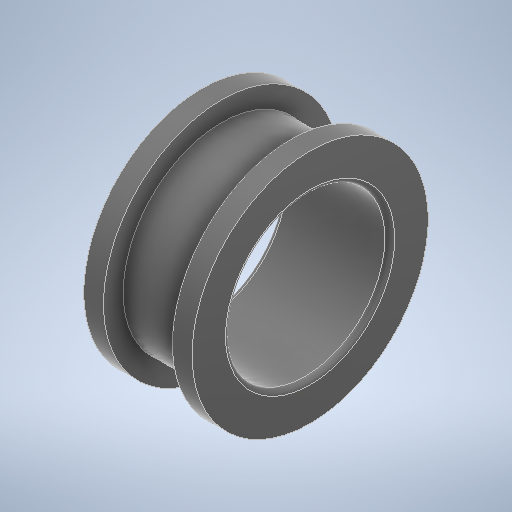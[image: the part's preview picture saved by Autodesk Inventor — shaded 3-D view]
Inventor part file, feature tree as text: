
AUTODESK INVENTOR PART (.ipt)
format: ipt  version: 2025.1 (Build 291241020, 241B)  size: 620,544 bytes
history: native  units: mm
features: revolve x1, mirror x1, fillet x1, sketch x1
ambient origin geometry x8: Origin, YZ Plane, XZ Plane, XY Plane, X Axis, Y Axis, Z Axis, Center Point
bodies: Solid1 (feature_tree)
feature tree (4):
  revolve  "Revolution1"  [1 undecoded]
  mirror  "Mirror2"
  fillet  "Fillet1"  Radius=10.0mm
  sketch  "Sketch1"  dims[d0=5.5mm d1=3.5mm d2=10.0mm d3=12.0mm d4=8.1mm d5=360.0deg d8=1.0mm d9=0.5mm]
note: 1 required parameter value undecoded (feature->parameter linkage not recoverable at this tier; creation-order binding heuristic only, values carry confidence <= 0.55)
